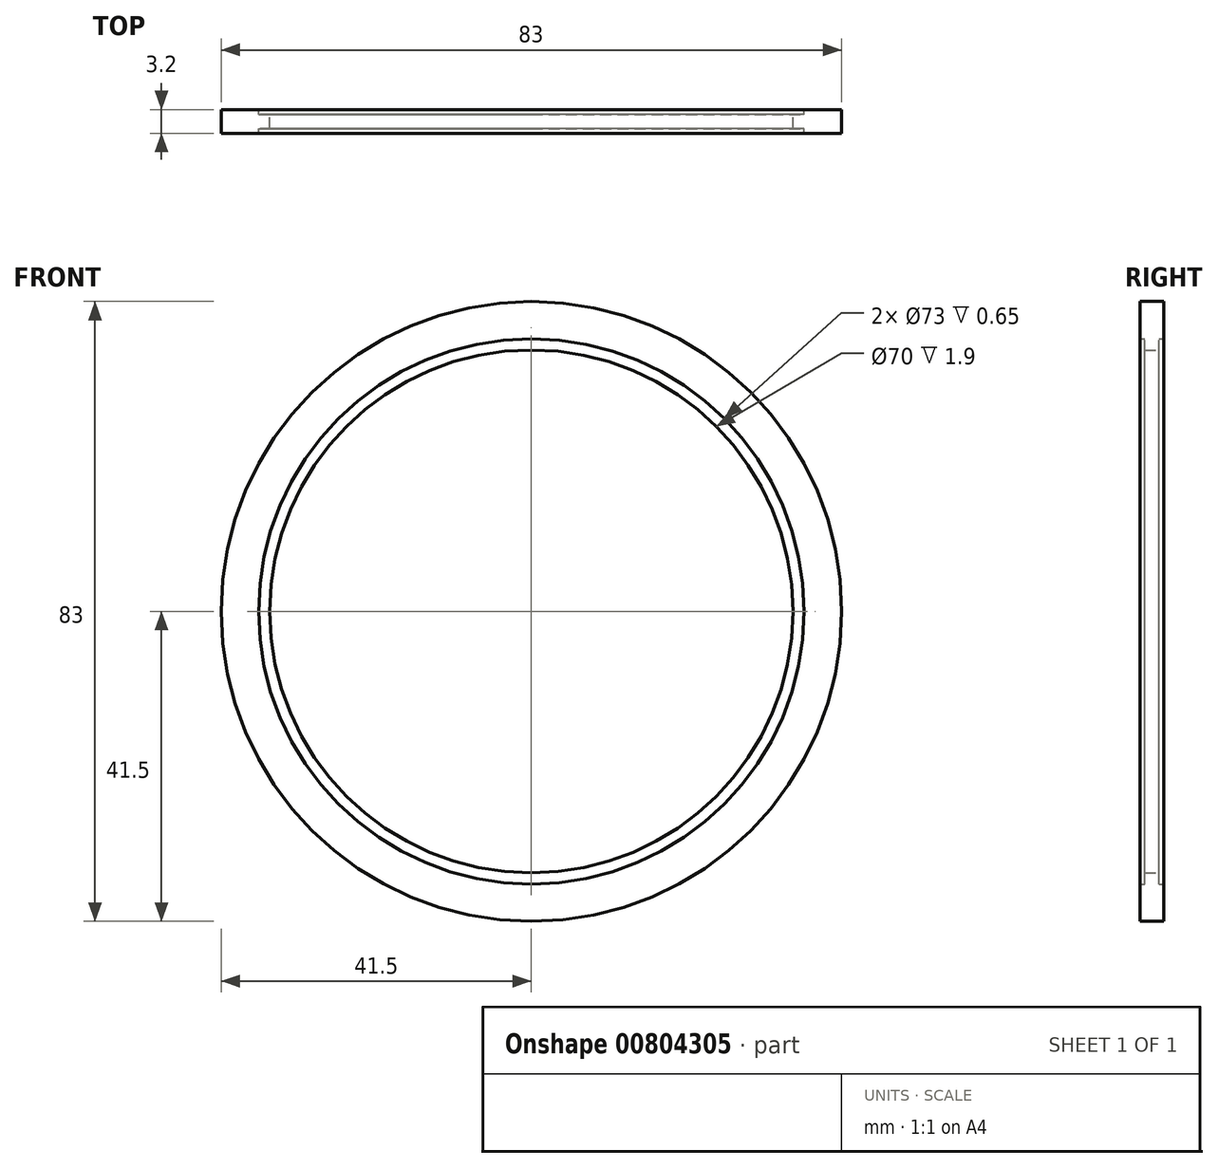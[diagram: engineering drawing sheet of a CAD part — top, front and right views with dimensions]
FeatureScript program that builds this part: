
annotation { "Feature Type Name" : "Feature", "Feature Type Description" : "" }
export const myFeature = defineFeature(function(context is Context, id is Id, definition is map)
    precondition{}
    {
        {
            var Q0;
            Q0=qCreatedBy(makeId("Front.planeOp"),FACE);
            var sketch = newSketch(context, id + "F0", { "sketchPlane" : qUnion([Q0])});
            skCircle(sketch, "E0", {"center": v(0, 0) * mm, "radius": 41.5 * mm});
            skCircle(sketch, "E1", {"center": v(0, 0) * mm, "radius": 36.5 * mm});
            skSolve(sketch);
        }
        {
            var Q0;
            Q0=makeQuery(id+"F0.imprint","IMPRINT",FACE,{"disambiguationData":[TD([[makeQuery(id+"F0.imprint","IMPRINT",EDGE,{"derivedFrom":sQuery(id+"F0.wireOp",EDGE,"E0")}),1.0]])]});
            extrude(context, id + "F1", {"entities" : qUnion([Q0]), "endBound" : BoundingType.SYMMETRIC, "depth" : 3.2 * mm, "offsetDistance" : 25 * mm});
        }
        {
            var Q0;
            Q0=qCreatedBy(makeId("Front.planeOp"),FACE);
            var sketch = newSketch(context, id + "F2", { "sketchPlane" : qUnion([Q0])});
            skCircle(sketch, "E2", {"center": v(0, 0) * mm, "radius": 35 * mm});
            skCircle(sketch, "E3", {"center": v(0, 0) * mm, "radius": 36.5 * mm});
            skSolve(sketch);
        }
        {
            var Q0;
            Q0=makeQuery(id+"F2.imprint","IMPRINT",FACE,{"disambiguationData":[TD([[makeQuery(id+"F2.imprint","IMPRINT",EDGE,{"derivedFrom":sQuery(id+"F2.wireOp",EDGE,"E2")}),-1.0]])]});
            extrude(context, id + "F3", {"entities" : qUnion([Q0]), "operationType" : NewBodyOperationType.ADD, "endBound" : BoundingType.SYMMETRIC, "depth" : (3.2 - (2 * 0.65)) * mm, "offsetDistance" : 25 * mm});
        }
    });
